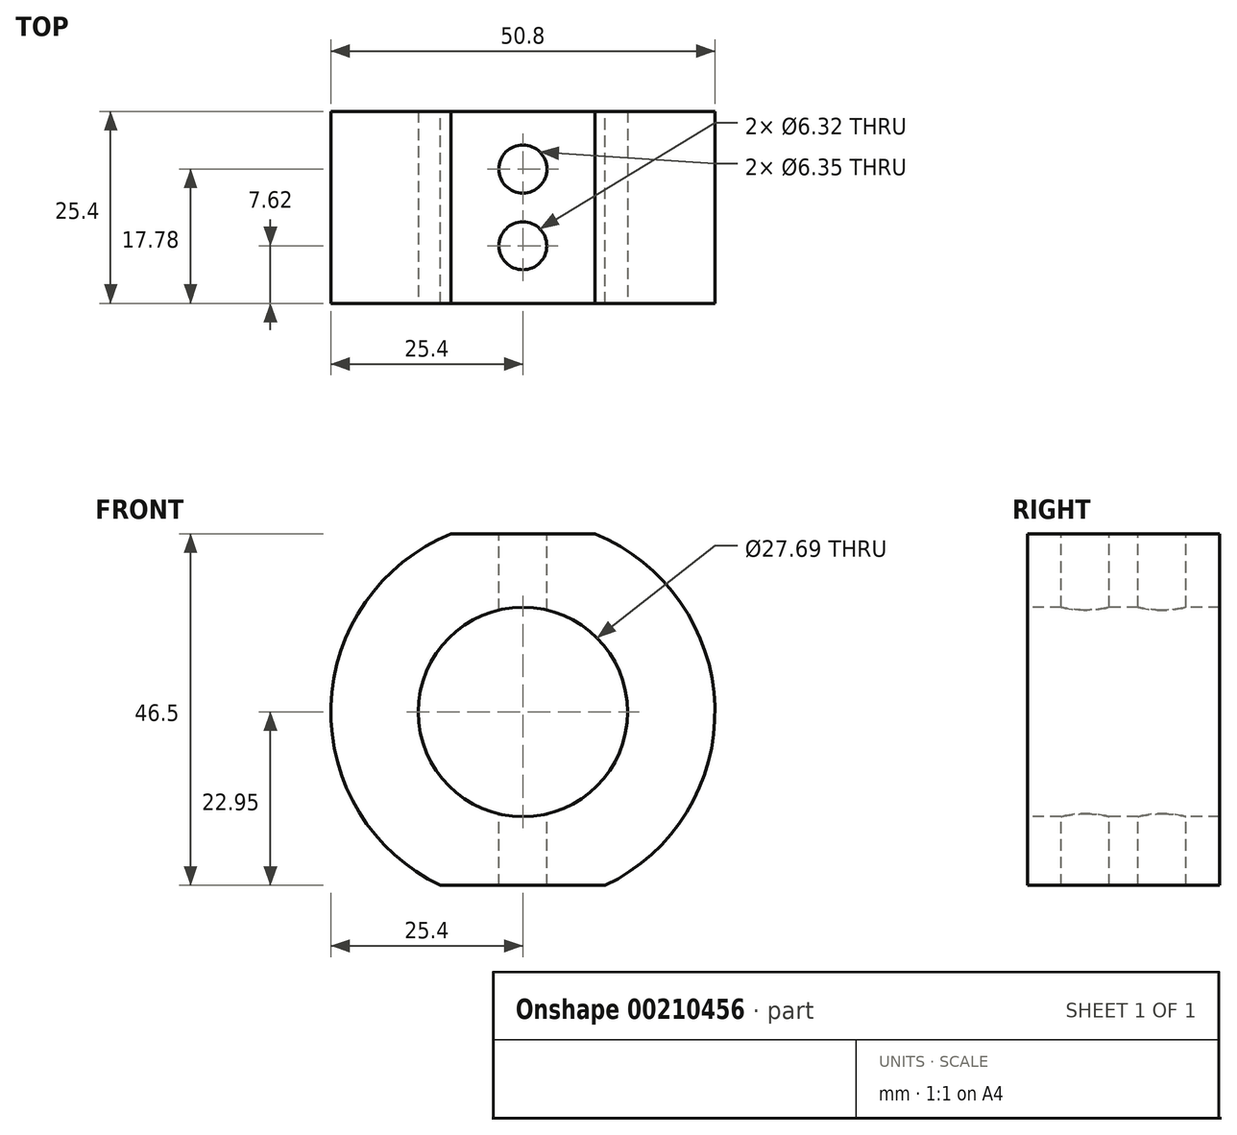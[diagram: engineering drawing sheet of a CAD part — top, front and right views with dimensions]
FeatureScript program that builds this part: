
annotation { "Feature Type Name" : "Feature", "Feature Type Description" : "" }
export const myFeature = defineFeature(function(context is Context, id is Id, definition is map)
    precondition{}
    {
        {
            var Q0;
            Q0=qCreatedBy(makeId("Front.planeOp"),FACE);
            var sketch = newSketch(context, id + "F0", { "sketchPlane" : qUnion([Q0])});
            skArc(sketch, "E0", {"start": v(-9.53, 23.55) * mm, "mid": v(-25.39, 0.74) * mm, "end": v(-10.89, -22.95) * mm});
            skCircle(sketch, "E1", {"center": v(0, 0) * mm, "radius": 1.59 * mm});
            skLineSegment(sketch, "E2.bottom", {"start": v(-9.53, 23.55) * mm, "end": v(9.52, 23.55) * mm});
            skLineSegment(sketch, "E2.top", {"start": v(-10.89, -22.95) * mm, "end": v(10.89, -22.95) * mm});
            skArc(sketch, "E3.trimOffspring", {"start": v(10.89, -22.95) * mm, "mid": v(25.39, 0.74) * mm, "end": v(9.52, 23.55) * mm});
            skSolve(sketch);
        }
        {
            var Q0;
            Q0 = qSketchRegion(id + "F0", true);
            extrude(context, id + "F1", {"entities" : qUnion([Q0]), "depth" : 25.4 * mm});
        }
        {
            var Q0;
            Q0=makeQuery(id+"F1.opExtrude","SWEPT_FACE",FACE,{"disambiguationData":[OSD([sQuery(id+"F0.wireOp",EDGE,"E2.bottom")])]});
            var sketch = newSketch(context, id + "F2", { "sketchPlane" : qUnion([Q0])});
            skCircle(sketch, "E4", {"center": v(0, -7.62) * mm, "radius": 3.18 * mm});
            skCircle(sketch, "E5", {"center": v(0, -17.78) * mm, "radius": 3.16 * mm});
            skSolve(sketch);
        }
        {
            var Q0;
            Q0 = qSketchRegion(id + "F2", true);
            extrude(context, id + "F3", {"entities" : qUnion([Q0]), "operationType" : NewBodyOperationType.REMOVE, "endBound" : BoundingType.THROUGH_ALL, "oppositeDirection" : true, "depth" : 25.4 * mm});
        }
        {
            var Q0;
            Q0=makeQuery(id+"F1.opExtrude","CAP_FACE",FACE,{"disambiguationData":[OSD([sQuery(id+"F0.wireOp",EDGE,"E0"),sQuery(id+"F0.wireOp",EDGE,"E1"),sQuery(id+"F0.wireOp",EDGE,"E2.bottom"),sQuery(id+"F0.wireOp",EDGE,"E2.top"),sQuery(id+"F0.wireOp",EDGE,"E3.trimOffspring")])],"isStart":false});
            var sketch = newSketch(context, id + "F4", { "sketchPlane" : qUnion([Q0])});
            skCircle(sketch, "E6", {"center": v(0, 0) * mm, "radius": 13.84 * mm});
            skSolve(sketch);
        }
        {
            var Q0;
            Q0 = qSketchRegion(id + "F4", true);
            extrude(context, id + "F5", {"entities" : qUnion([Q0]), "operationType" : NewBodyOperationType.REMOVE, "endBound" : BoundingType.THROUGH_ALL, "oppositeDirection" : true, "depth" : 25.4 * mm});
        }
    });
